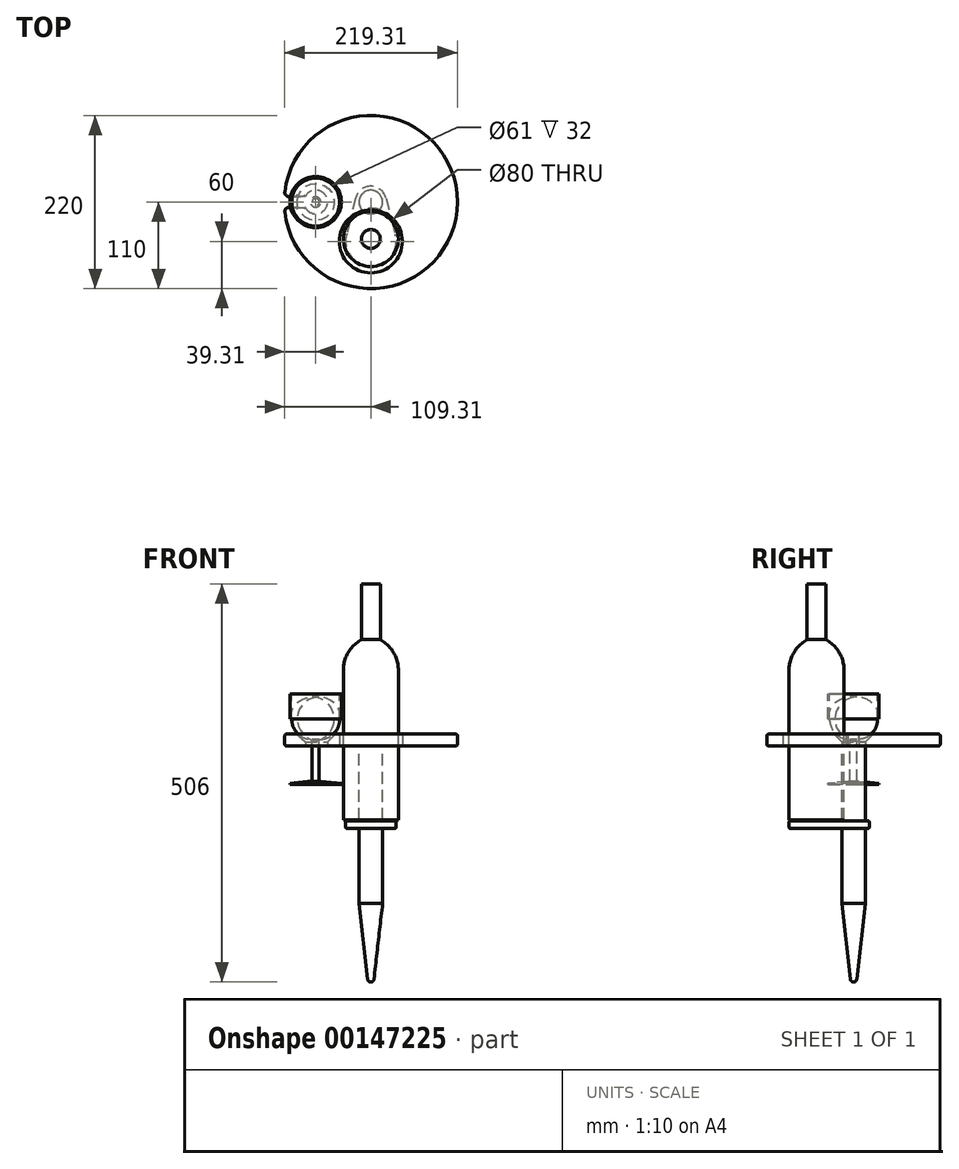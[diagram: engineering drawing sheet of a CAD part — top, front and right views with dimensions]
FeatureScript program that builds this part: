
annotation { "Feature Type Name" : "Feature", "Feature Type Description" : "" }
export const myFeature = defineFeature(function(context is Context, id is Id, definition is map)
    precondition{}
    {
        {
            var Q0;
            Q0=qCreatedBy(makeId("Top.planeOp"),FACE);
            var sketch = newSketch(context, id + "F0", { "sketchPlane" : qUnion([Q0])});
            skCircle(sketch, "E0", {"center": v(0, -50) * mm, "radius": 40 * mm});
            skLineSegment(sketch, "E1", {"start": v(-70, 0) * mm, "end": v(70, 0) * mm, "construction": true});
            skCircle(sketch, "E2", {"center": v(0, 0) * mm, "radius": 110 * mm});
            skLineSegment(sketch, "E3", {"start": v(0, -50) * mm, "end": v(0, 0) * mm, "construction": true});
            skSolve(sketch);
        }
        {
            var Q0;
            Q0=makeQuery(id+"F0.imprint","IMPRINT",FACE,{"disambiguationData":[TD([[makeQuery(id+"F0.imprint","IMPRINT",EDGE,{"derivedFrom":sQuery(id+"F0.wireOp",EDGE,"E0")}),-1.0]])]});
            extrude(context, id + "F1", {"entities" : qUnion([Q0]), "depth" : 15 * mm});
        }
        {
            var Q0;
            Q0=qCreatedBy(makeId("Top.planeOp"),FACE);
            var sketch = newSketch(context, id + "F2", { "sketchPlane" : qUnion([Q0])});
            skArc(sketch, "E4", {"start": v(-83.27, -7) * mm, "mid": v(-55, 0) * mm, "end": v(-83.27, 7) * mm});
            skLineSegment(sketch, "E5.bottom", {"start": v(-128.27, -7) * mm, "end": v(-83.27, -7) * mm});
            skLineSegment(sketch, "E5.top", {"start": v(-128.27, 7) * mm, "end": v(-83.27, 7) * mm});
            skLineSegment(sketch, "E5.left", {"start": v(-128.27, -7) * mm, "end": v(-128.27, 7) * mm});
            skLineSegment(sketch, "E6", {"start": v(-70, 0) * mm, "end": v(0, 0) * mm, "construction": true});
            skLineSegment(sketch, "E7", {"start": v(-70, 0) * mm, "end": v(-128.27, 0) * mm, "construction": true});
            skSolve(sketch);
        }
        {
            var Q0;
            Q0 = qSketchRegion(id + "F2", true);
            extrude(context, id + "F3", {"entities" : qUnion([Q0]), "operationType" : NewBodyOperationType.REMOVE, "endBound" : BoundingType.THROUGH_ALL, "depth" : 25 * mm});
        }
        {
            var Q0;
            Q0=qCreatedBy(makeId("Front.planeOp"),FACE);
            var sketch = newSketch(context, id + "F4", { "sketchPlane" : qUnion([Q0])});
            skLineSegment(sketch, "E8", {"start": v(0, 0) * mm, "end": v(0, 78.75) * mm, "construction": true});
            skSolve(sketch);
        }
        {
            var Q0;
            Q0=makeQuery(id+"F3.boolean.opBoolean","INTERSECT",EDGE,{"derivedFrom":[makeQuery(id+"F1.opExtrude","CAP_FACE",FACE,{"disambiguationData":[OSD([sQuery(id+"F0.wireOp",EDGE,"E0"),sQuery(id+"F0.wireOp",EDGE,"E2")])],"isStart":false}),makeQuery(id+"F3.opExtrude","SWEPT_FACE",FACE,{"disambiguationData":[OSD([sQuery(id+"F2.wireOp",EDGE,"E4")])]})]});
            chamfer(context, id + "F5", {"entities" : qUnion([Q0]), "width" : 10 * mm, "tangentPropagation" : true});
        }
        {
            var Q0;
            Q0=makeQuery(id+"F3.boolean.opBoolean","INTERSECT",EDGE,{"derivedFrom":[makeQuery(id+"F1.opExtrude","SWEPT_FACE",FACE,{"disambiguationData":[OSD([sQuery(id+"F0.wireOp",EDGE,"E2")])]}),makeQuery(id+"F3.opExtrude","SWEPT_FACE",FACE,{"disambiguationData":[OSD([sQuery(id+"F2.wireOp",EDGE,"E5.top")])]})]});
            var Q1;
            Q1=makeQuery(id+"F3.boolean.opBoolean","INTERSECT",EDGE,{"derivedFrom":[makeQuery(id+"F1.opExtrude","SWEPT_FACE",FACE,{"disambiguationData":[OSD([sQuery(id+"F0.wireOp",EDGE,"E2")])]}),makeQuery(id+"F3.opExtrude","SWEPT_FACE",FACE,{"disambiguationData":[OSD([sQuery(id+"F2.wireOp",EDGE,"E5.bottom")])]})]});
            fillet(context, id + "F6", {"entities" : qUnion([Q0, Q1]), "radius" : 5 * mm, "tangentPropagation" : true, "allowEdgeOverflow" : false});
        }
        {
            var Q0;
            Q0=makeQuery(id+"F1.opExtrude","CAP_FACE",FACE,{"disambiguationData":[OSD([sQuery(id+"F0.wireOp",EDGE,"E0"),sQuery(id+"F0.wireOp",EDGE,"5pv25lc3-jAKO-7TQt-mW91-OiMwdfcbpWFd"),sQuery(id+"F0.wireOp",EDGE,"xdOFlgZJ-Q9ej-jgwB-Z53N-QYi1P9MyNLaz"),sQuery(id+"F0.wireOp",EDGE,"8ed96047-2d13-4c78-9651-4d1e828075b11"),sQuery(id+"F0.wireOp",EDGE,"7d6c8b58-936c-4b81-ae2c-2cd44cd883682"),sQuery(id+"F0.wireOp",EDGE,"13d03626-8b59-418c-8978-8058052f28d91"),sQuery(id+"F0.wireOp",EDGE,"e3eefbaf-872d-479d-9db3-40dda04d0e38"),sQuery(id+"F0.wireOp",EDGE,"x9pFfLyk-mST7-FCjy-Jf6b-LapPgMCKo5VM"),sQuery(id+"F0.wireOp",EDGE,"eRyap1mk-bSg4-b9OP-0ZbS-HXspzodv7Jz1")])],"isStart":false});
            var Q1;
            Q1=makeQuery(id+"F1.opExtrude","CAP_FACE",FACE,{"disambiguationData":[OSD([sQuery(id+"F0.wireOp",EDGE,"E0"),sQuery(id+"F0.wireOp",EDGE,"5pv25lc3-jAKO-7TQt-mW91-OiMwdfcbpWFd"),sQuery(id+"F0.wireOp",EDGE,"xdOFlgZJ-Q9ej-jgwB-Z53N-QYi1P9MyNLaz"),sQuery(id+"F0.wireOp",EDGE,"8ed96047-2d13-4c78-9651-4d1e828075b11"),sQuery(id+"F0.wireOp",EDGE,"7d6c8b58-936c-4b81-ae2c-2cd44cd883682"),sQuery(id+"F0.wireOp",EDGE,"13d03626-8b59-418c-8978-8058052f28d91"),sQuery(id+"F0.wireOp",EDGE,"e3eefbaf-872d-479d-9db3-40dda04d0e38"),sQuery(id+"F0.wireOp",EDGE,"x9pFfLyk-mST7-FCjy-Jf6b-LapPgMCKo5VM"),sQuery(id+"F0.wireOp",EDGE,"eRyap1mk-bSg4-b9OP-0ZbS-HXspzodv7Jz1")])],"isStart":true});
            fillet(context, id + "F7", {"entities" : qUnion([Q0, Q1]), "radius" : 2 * mm, "tangentPropagation" : true, "allowEdgeOverflow" : false});
        }
        {
            var Q0;
            Q0=qCreatedBy(makeId("Front.planeOp"),FACE);
            var sketch = newSketch(context, id + "F8", { "sketchPlane" : qUnion([Q0])});
            skLineSegment(sketch, "E9.bottom", {"start": v(0, 0) * mm, "end": v(-15, 0) * mm});
            skLineSegment(sketch, "E9.left", {"start": v(0, 0) * mm, "end": v(0, -300) * mm});
            skLineSegment(sketch, "E9.right", {"start": v(-15, 0) * mm, "end": v(-15, -200) * mm});
            skLineSegment(sketch, "E10", {"start": v(0, -300) * mm, "end": v(28.15, -300) * mm, "construction": true});
            skLineSegment(sketch, "E11", {"start": v(-15, -200) * mm, "end": v(-3.97, -296.45) * mm});
            skArc(sketch, "E12", {"start": v(-3.97, -296.45) * mm, "mid": v(-2.66, -298.98) * mm, "end": v(0, -300) * mm});
            skSolve(sketch);
        }
        {
            var Q0;
            Q0 = qSketchRegion(id + "F8", true);
            var Q1;
            Q1=sQuery(id+"F8.wireOp",EDGE,"E9.left");
            revolve(context, id + "F9", {"operationType" : NewBodyOperationType.ADD, "entities" : qUnion([Q0]), "axis" : qUnion([Q1]), "revolveType" : RevolveType.FULL});
        }
        {
            var Q0;
            Q0=makeQuery(id+"F1.opExtrude","CAP_FACE",FACE,{"disambiguationData":[OSD([sQuery(id+"F0.wireOp",EDGE,"E0"),sQuery(id+"F0.wireOp",EDGE,"5pv25lc3-jAKO-7TQt-mW91-OiMwdfcbpWFd"),sQuery(id+"F0.wireOp",EDGE,"xdOFlgZJ-Q9ej-jgwB-Z53N-QYi1P9MyNLaz"),sQuery(id+"F0.wireOp",EDGE,"8ed96047-2d13-4c78-9651-4d1e828075b11"),sQuery(id+"F0.wireOp",EDGE,"7d6c8b58-936c-4b81-ae2c-2cd44cd883682"),sQuery(id+"F0.wireOp",EDGE,"13d03626-8b59-418c-8978-8058052f28d91"),sQuery(id+"F0.wireOp",EDGE,"e3eefbaf-872d-479d-9db3-40dda04d0e38"),sQuery(id+"F0.wireOp",EDGE,"x9pFfLyk-mST7-FCjy-Jf6b-LapPgMCKo5VM"),sQuery(id+"F0.wireOp",EDGE,"eRyap1mk-bSg4-b9OP-0ZbS-HXspzodv7Jz1")])],"isStart":true});
            cPlane(context, id + "F10", {"entities" : qUnion([Q0]), "cplaneType" : CPlaneType.OFFSET, "offset" : 95 * mm, "width" : 150 * mm, "height" : 150 * mm});
        }
        {
            var Q0;
            Q0=qCreatedBy(id+"F10.planeOp",FACE);
            var sketch = newSketch(context, id + "F11", { "sketchPlane" : qUnion([Q0])});
            skLineSegment(sketch, "E13.left", {"start": v(-19.42, -4.8) * mm, "end": v(-31.06, 42.32) * mm});
            skLineSegment(sketch, "E13.right", {"start": v(19.42, -4.8) * mm, "end": v(31.06, 42.32) * mm});
            skArc(sketch, "E14", {"start": v(-19.42, -4.8) * mm, "mid": v(0, -20) * mm, "end": v(19.42, -4.8) * mm});
            skArc(sketch, "E15", {"start": v(31.06, 42.32) * mm, "mid": v(0, 82) * mm, "end": v(-31.06, 42.32) * mm});
            skCircle(sketch, "E16.0", {"center": v(0, 0) * mm, "radius": 15 * mm});
            skSolve(sketch);
        }
        {
            var Q0;
            Q0 = qSketchRegion(id + "F11", true);
            extrude(context, id + "F12", {"entities" : qUnion([Q0]), "operationType" : NewBodyOperationType.ADD, "depth" : 10 * mm});
        }
        {
            var Q0;
            Q0=makeQuery(id+"F12.opExtrude","CAP_EDGE",EDGE,{"disambiguationData":[OSD([sQuery(id+"F11.wireOp",EDGE,"E15")])],"isStart":true});
            var Q1;
            Q1=makeQuery(id+"F12.opExtrude","CAP_EDGE",EDGE,{"disambiguationData":[OSD([sQuery(id+"F11.wireOp",EDGE,"E15")])],"isStart":false});
            fillet(context, id + "F13", {"entities" : qUnion([Q0, Q1]), "radius" : 2 * mm, "tangentPropagation" : true, "allowEdgeOverflow" : false});
        }
        {
            var Q0;
            Q0=qCreatedBy(makeId("Right.planeOp"),FACE);
            var sketch = newSketch(context, id + "F14", { "sketchPlane" : qUnion([Q0])});
            skLineSegment(sketch, "E17", {"start": v(-12, -94) * mm, "end": v(-47, -94) * mm});
            skLineSegment(sketch, "E18", {"start": v(-12, -94) * mm, "end": v(-12, 96) * mm});
            skLineSegment(sketch, "E19", {"start": v(-35, 135) * mm, "end": v(-35, 206) * mm});
            skLineSegment(sketch, "E20", {"start": v(-47, 206) * mm, "end": v(-35, 206) * mm});
            skLineSegment(sketch, "E21", {"start": v(-47, 206) * mm, "end": v(-47, -94) * mm});
            skArc(sketch, "E22", {"start": v(-12, 96) * mm, "mid": v(-18.18, 118.64) * mm, "end": v(-35, 135) * mm});
            skLineSegment(sketch, "E23", {"start": v(-10, 13) * mm, "end": v(-10, 2) * mm, "construction": true});
            skLineSegment(sketch, "E24", {"start": v(-90, 2) * mm, "end": v(-90, 13) * mm, "construction": true});
            skSolve(sketch);
        }
        {
            var Q0;
            Q0 = qSketchRegion(id + "F14", true);
            var Q1;
            Q1=sQuery(id+"F14.wireOp",EDGE,"E21");
            revolve(context, id + "F15", {"entities" : qUnion([Q0]), "axis" : qUnion([Q1]), "revolveType" : RevolveType.FULL});
        }
        {
            var Q0;
            Q0=qCreatedBy(makeId("Front.planeOp"),FACE);
            var sketch = newSketch(context, id + "F16", { "sketchPlane" : qUnion([Q0])});
            skLineSegment(sketch, "E25", {"start": v(-70, -48.9) * mm, "end": v(-37.5, -48.9) * mm});
            skLineSegment(sketch, "E26", {"start": v(-37.5, -48.9) * mm, "end": v(-37.5, -44.9) * mm});
            skLineSegment(sketch, "E27", {"start": v(-37.5, -44.9) * mm, "end": v(-65.5, -44.9) * mm});
            skLineSegment(sketch, "E28", {"start": v(-37.5, 34.1) * mm, "end": v(-37.5, 66.1) * mm});
            skLineSegment(sketch, "E29", {"start": v(-37.5, 66.1) * mm, "end": v(-39.5, 66.1) * mm});
            skLineSegment(sketch, "E30", {"start": v(-65.5, -44.9) * mm, "end": v(-65.5, 6.1) * mm});
            skLineSegment(sketch, "E31", {"start": v(-65.5, 6.1) * mm, "end": v(-70, 6.1) * mm, "construction": true});
            skArc(sketch, "E32", {"start": v(-65.5, 6.1) * mm, "mid": v(-45.7, 14.3) * mm, "end": v(-37.5, 34.1) * mm});
            skLineSegment(sketch, "E33", {"start": v(-45.59, 14.41) * mm, "end": v(-55, 5) * mm, "construction": true});
            skLineSegment(sketch, "E34.0", {"start": v(-39.5, 34.1) * mm, "end": v(-39.5, 66.1) * mm});
            skArc(sketch, "E34.1", {"start": v(-65.5, 8.1) * mm, "mid": v(-47.12, 15.71) * mm, "end": v(-39.5, 34.1) * mm});
            skLineSegment(sketch, "E35", {"start": v(-65.5, 8.1) * mm, "end": v(-70, 8.1) * mm});
            skLineSegment(sketch, "E36", {"start": v(-70, 8.1) * mm, "end": v(-70, -48.9) * mm});
            skSolve(sketch);
        }
        {
            var Q0;
            Q0 = qSketchRegion(id + "F16", true);
            var Q1;
            Q1=sQuery(id+"F16.wireOp",EDGE,"E36");
            revolve(context, id + "F17", {"entities" : qUnion([Q0]), "axis" : qUnion([Q1]), "revolveType" : RevolveType.FULL});
        }
        {
            var Q0;
            Q0=makeQuery(id+"F17.opRevolve","SWEPT_EDGE",EDGE,{"disambiguationData":[OSD([sQuery(id+"F16.wireOp",EDGE,"E26"),sQuery(id+"F16.wireOp",EDGE,"E27")])]});
            chamfer(context, id + "F18", {"entities" : qUnion([Q0]), "chamferType" : ChamferType.TWO_OFFSETS, "width1" : 26 * mm, "oppositeDirection" : false, "width2" : 3 * mm, "tangentPropagation" : true});
        }
    });
